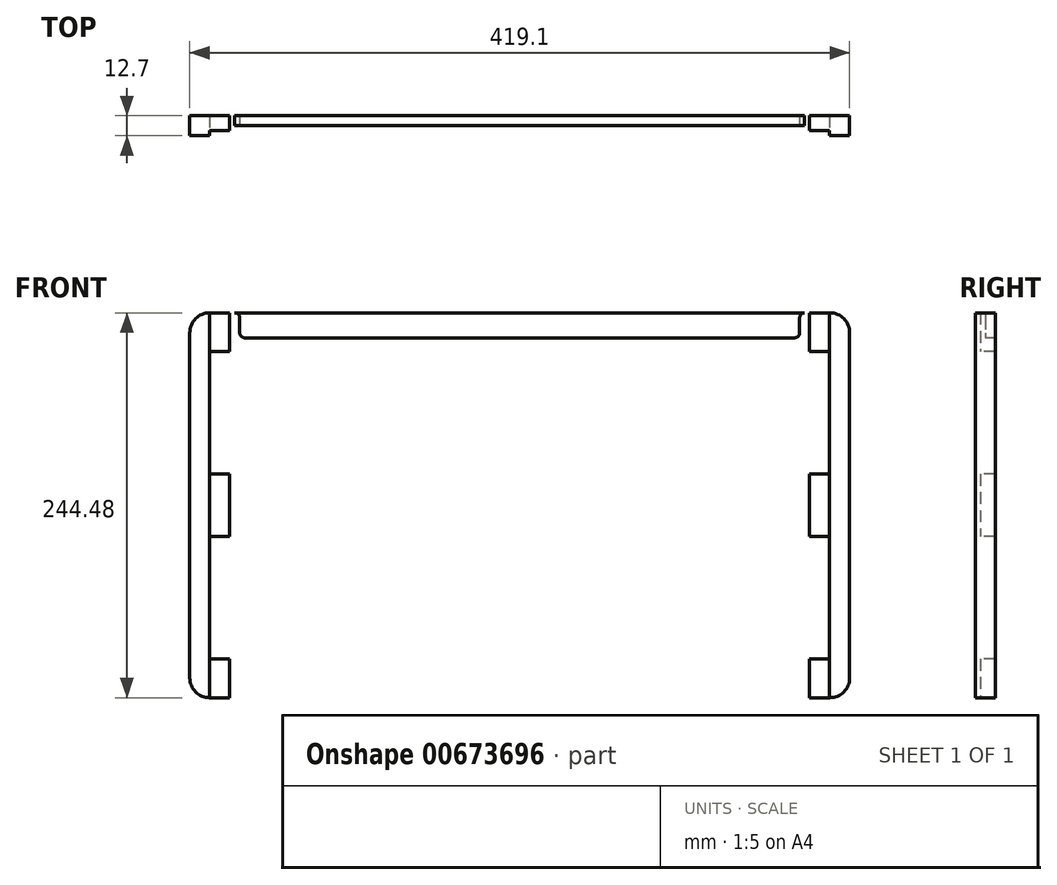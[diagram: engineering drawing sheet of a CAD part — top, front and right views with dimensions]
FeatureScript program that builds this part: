
annotation { "Feature Type Name" : "Feature", "Feature Type Description" : "" }
export const myFeature = defineFeature(function(context is Context, id is Id, definition is map)
    precondition{}
    {
        {
            var Q0;
            Q0=qCreatedBy(makeId("Front.planeOp"),FACE);
            var sketch = newSketch(context, id + "F0", { "sketchPlane" : qUnion([Q0])});
            skLineSegment(sketch, "E0.bottom", {"start": v(-196.85, 122.24) * mm, "end": v(-180.98, 122.24) * mm});
            skLineSegment(sketch, "E0.top", {"start": v(-196.85, -122.24) * mm, "end": v(196.85, -122.24) * mm});
            skLineSegment(sketch, "E0.left", {"start": v(-209.55, 109.54) * mm, "end": v(-209.55, -109.54) * mm});
            skLineSegment(sketch, "E0.right", {"start": v(209.55, 109.54) * mm, "end": v(209.55, -109.54) * mm});
            skPoint(sketch, "E0.middle", {"position": v(0, 0) * mm});
            skLineSegment(sketch, "E1", {"start": v(0, 122.24) * mm, "end": v(0, -122.24) * mm, "construction": true});
            skLineSegment(sketch, "E2", {"start": v(209.55, 0) * mm, "end": v(-209.55, 0) * mm, "construction": true});
            skLineSegment(sketch, "E3.left", {"start": v(-184.15, 122.24) * mm, "end": v(-184.15, -122.24) * mm});
            skLineSegment(sketch, "E3.right", {"start": v(184.15, 122.24) * mm, "end": v(184.15, -122.24) * mm});
            skLineSegment(sketch, "E4.bottom", {"start": v(-184.15, 97.63) * mm, "end": v(-196.85, 97.63) * mm});
            skLineSegment(sketch, "E4.top", {"start": v(-184.15, 19.84) * mm, "end": v(-196.85, 19.84) * mm});
            skLineSegment(sketch, "E4.left", {"start": v(-184.15, 97.63) * mm, "end": v(-184.15, 19.84) * mm});
            skLineSegment(sketch, "E4.right", {"start": v(-196.85, 97.63) * mm, "end": v(-196.85, 19.84) * mm});
            skLineSegment(sketch, "E5.MirrorCS", {"start": v(-184.15, -97.63) * mm, "end": v(-196.85, -97.63) * mm});
            skLineSegment(sketch, "E6.MirrorCS", {"start": v(-184.15, -19.84) * mm, "end": v(-196.85, -19.84) * mm});
            skLineSegment(sketch, "E7.MirrorCS", {"start": v(-184.15, -97.63) * mm, "end": v(-184.15, -19.84) * mm});
            skLineSegment(sketch, "E8.MirrorCS", {"start": v(-196.85, -97.63) * mm, "end": v(-196.85, -19.84) * mm});
            skLineSegment(sketch, "E9.MirrorCS", {"start": v(184.15, -97.63) * mm, "end": v(196.85, -97.63) * mm});
            skLineSegment(sketch, "E10.MirrorCS", {"start": v(196.85, 97.63) * mm, "end": v(196.85, 19.84) * mm});
            skLineSegment(sketch, "E11.MirrorCS", {"start": v(184.15, 97.63) * mm, "end": v(184.15, 19.84) * mm});
            skLineSegment(sketch, "E12.MirrorCS", {"start": v(184.15, -19.84) * mm, "end": v(196.85, -19.84) * mm});
            skLineSegment(sketch, "E13.MirrorCS", {"start": v(184.15, 19.84) * mm, "end": v(196.85, 19.84) * mm});
            skLineSegment(sketch, "E14.MirrorCS", {"start": v(184.15, -97.63) * mm, "end": v(184.15, -19.84) * mm});
            skLineSegment(sketch, "E15.MirrorCS", {"start": v(196.85, -97.63) * mm, "end": v(196.85, -19.84) * mm});
            skLineSegment(sketch, "E16.MirrorCS", {"start": v(184.15, 97.63) * mm, "end": v(196.85, 97.63) * mm});
            skPoint(sketch, "E17.visualSharp", {"position": v(-209.55, 122.24) * mm});
            skArc(sketch, "E17.filletArc", {"start": v(-196.85, 122.24) * mm, "mid": v(-205.83, 118.52) * mm, "end": v(-209.55, 109.54) * mm});
            skPoint(sketch, "E18.visualSharp", {"position": v(-209.55, -122.24) * mm});
            skArc(sketch, "E18.filletArc", {"start": v(-209.55, -109.54) * mm, "mid": v(-205.83, -118.52) * mm, "end": v(-196.85, -122.24) * mm});
            skPoint(sketch, "E19.visualSharp", {"position": v(209.55, -122.24) * mm});
            skArc(sketch, "E19.filletArc", {"start": v(196.85, -122.24) * mm, "mid": v(205.83, -118.52) * mm, "end": v(209.55, -109.54) * mm});
            skPoint(sketch, "E20.visualSharp", {"position": v(209.55, 122.24) * mm});
            skArc(sketch, "E20.filletArc", {"start": v(209.55, 109.54) * mm, "mid": v(205.83, 118.52) * mm, "end": v(196.85, 122.24) * mm});
            skLineSegment(sketch, "E21.top", {"start": v(-174.62, 106.36) * mm, "end": v(174.62, 106.36) * mm});
            skLineSegment(sketch, "E21.left", {"start": v(-177.8, 119.06) * mm, "end": v(-177.8, 109.54) * mm});
            skLineSegment(sketch, "E21.right", {"start": v(177.8, 119.06) * mm, "end": v(177.8, 109.54) * mm});
            skPoint(sketch, "E22.visualSharp", {"position": v(-177.8, 106.36) * mm});
            skArc(sketch, "E22.filletArc", {"start": v(-177.8, 109.54) * mm, "mid": v(-176.87, 107.3) * mm, "end": v(-174.62, 106.36) * mm});
            skArc(sketch, "E23.filletArc", {"start": v(-177.8, 119.06) * mm, "mid": v(-178.73, 121.3) * mm, "end": v(-180.98, 122.24) * mm});
            skPoint(sketch, "E24.visualSharp", {"position": v(177.8, 106.36) * mm});
            skArc(sketch, "E24.filletArc", {"start": v(174.62, 106.36) * mm, "mid": v(176.87, 107.3) * mm, "end": v(177.8, 109.54) * mm});
            skLineSegment(sketch, "E25", {"start": v(180.98, 122.24) * mm, "end": v(196.85, 122.24) * mm});
            skPoint(sketch, "E26.visualSharp", {"position": v(177.8, 122.24) * mm});
            skArc(sketch, "E26.filletArc", {"start": v(180.98, 122.24) * mm, "mid": v(178.73, 121.3) * mm, "end": v(177.8, 119.06) * mm});
            skLineSegment(sketch, "E27", {"start": v(-180.98, 122.24) * mm, "end": v(180.98, 122.24) * mm});
            skLineSegment(sketch, "E28", {"start": v(196.85, 122.24) * mm, "end": v(196.85, -122.24) * mm});
            skLineSegment(sketch, "E29", {"start": v(-196.85, 122.24) * mm, "end": v(-196.85, -122.24) * mm});
            skSolve(sketch);
        }
        {
            var Q0;
            Q0=makeQuery(id+"F0.imprint","IMPRINT",FACE,{"disambiguationData":[TD([[makeQuery(id+"F0.imprint","IMPRINT",EDGE,{"derivedFrom":sQuery(id+"F0.wireOp",EDGE,"E0.left")}),1.0]])]});
            var Q1;
            {var subQ5=sQuery(id+"F0.wireOp",EDGE,"E4.bottom");Q1=makeQuery(id+"F0.imprint","IMPRINT",FACE,{"disambiguationData":[TD([[makeQuery(id+"F0.imprint","IMPRINT",EDGE,{"derivedFrom":subQ5}),-1.0]])]});}
            var Q2;
            {var subQ0=sQuery(id+"F0.wireOp",EDGE,"E6.MirrorCS");Q2=makeQuery(id+"F0.imprint","IMPRINT",FACE,{"disambiguationData":[TD([[makeQuery(id+"F0.imprint","IMPRINT",EDGE,{"derivedFrom":subQ0}),-1.0]])]});}
            var Q3;
            {var subQ5=sQuery(id+"F0.wireOp",EDGE,"E5.MirrorCS");Q3=makeQuery(id+"F0.imprint","IMPRINT",FACE,{"disambiguationData":[TD([[makeQuery(id+"F0.imprint","IMPRINT",EDGE,{"derivedFrom":subQ5}),1.0]])]});}
            var Q4;
            {var subQ0=sQuery(id+"F0.wireOp",EDGE,"E7.MirrorCS");Q4=makeQuery(id+"F0.imprint","IMPRINT",FACE,{"disambiguationData":[TD([[makeQuery(id+"F0.imprint","IMPRINT",EDGE,{"derivedFrom":subQ0}),-1.0]])]});}
            var Q5;
            {var subQ5=sQuery(id+"F0.wireOp",EDGE,"E9.MirrorCS");Q5=makeQuery(id+"F0.imprint","IMPRINT",FACE,{"disambiguationData":[TD([[makeQuery(id+"F0.imprint","IMPRINT",EDGE,{"derivedFrom":subQ5}),-1.0]])]});}
            var Q6;
            Q6=makeQuery(id+"F0.imprint","IMPRINT",FACE,{"disambiguationData":[TD([[makeQuery(id+"F0.imprint","IMPRINT",EDGE,{"derivedFrom":sQuery(id+"F0.wireOp",EDGE,"E0.right")}),-1.0]])]});
            var Q7;
            {var subQ0=sQuery(id+"F0.wireOp",EDGE,"E12.MirrorCS");Q7=makeQuery(id+"F0.imprint","IMPRINT",FACE,{"disambiguationData":[TD([[makeQuery(id+"F0.imprint","IMPRINT",EDGE,{"derivedFrom":subQ0}),1.0]])]});}
            var Q8;
            {var subQ3=sQuery(id+"F0.wireOp",EDGE,"E16.MirrorCS");Q8=makeQuery(id+"F0.imprint","IMPRINT",FACE,{"disambiguationData":[TD([[makeQuery(id+"F0.imprint","IMPRINT",EDGE,{"derivedFrom":subQ3}),1.0]])]});}
            var Q9;
            Q9=makeQuery(id+"F0.imprint","IMPRINT",FACE,{"disambiguationData":[TD([[makeQuery(id+"F0.imprint","IMPRINT",EDGE,{"derivedFrom":sQuery(id+"F0.wireOp",EDGE,"E21.top")}),1.0]])]});
            extrude(context, id + "F1", {"entities" : qUnion([Q0, Q1, Q2, Q3, Q4, Q5, Q6, Q7, Q8, Q9]), "oppositeDirection" : true, "depth" : 12.7 * mm, "offsetDistance" : 25.4 * mm});
        }
        {
            var Q0;
            {var subQ5=sQuery(id+"F0.wireOp",EDGE,"E5.MirrorCS");Q0=makeQuery(id+"F0.imprint","IMPRINT",FACE,{"disambiguationData":[TD([[makeQuery(id+"F0.imprint","IMPRINT",EDGE,{"derivedFrom":subQ5}),1.0]])]});}
            var Q1;
            {var subQ0=sQuery(id+"F0.wireOp",EDGE,"E6.MirrorCS");Q1=makeQuery(id+"F0.imprint","IMPRINT",FACE,{"disambiguationData":[TD([[makeQuery(id+"F0.imprint","IMPRINT",EDGE,{"derivedFrom":subQ0}),-1.0]])]});}
            var Q2;
            {var subQ5=sQuery(id+"F0.wireOp",EDGE,"E9.MirrorCS");Q2=makeQuery(id+"F0.imprint","IMPRINT",FACE,{"disambiguationData":[TD([[makeQuery(id+"F0.imprint","IMPRINT",EDGE,{"derivedFrom":subQ5}),-1.0]])]});}
            var Q3;
            {var subQ0=sQuery(id+"F0.wireOp",EDGE,"E12.MirrorCS");Q3=makeQuery(id+"F0.imprint","IMPRINT",FACE,{"disambiguationData":[TD([[makeQuery(id+"F0.imprint","IMPRINT",EDGE,{"derivedFrom":subQ0}),1.0]])]});}
            var Q4;
            {var subQ3=sQuery(id+"F0.wireOp",EDGE,"E16.MirrorCS");Q4=makeQuery(id+"F0.imprint","IMPRINT",FACE,{"disambiguationData":[TD([[makeQuery(id+"F0.imprint","IMPRINT",EDGE,{"derivedFrom":subQ3}),1.0]])]});}
            var Q5;
            {var subQ5=sQuery(id+"F0.wireOp",EDGE,"E4.bottom");Q5=makeQuery(id+"F0.imprint","IMPRINT",FACE,{"disambiguationData":[TD([[makeQuery(id+"F0.imprint","IMPRINT",EDGE,{"derivedFrom":subQ5}),-1.0]])]});}
            extrude(context, id + "F2", {"entities" : qUnion([Q0, Q1, Q2, Q3, Q4, Q5]), "operationType" : NewBodyOperationType.REMOVE, "oppositeDirection" : true, "depth" : 3.17 * mm, "offsetDistance" : 25.4 * mm});
        }
        {
            var Q0;
            Q0=makeQuery(id+"F0.imprint","IMPRINT",FACE,{"disambiguationData":[TD([[makeQuery(id+"F0.imprint","IMPRINT",EDGE,{"derivedFrom":sQuery(id+"F0.wireOp",EDGE,"E21.top")}),1.0]])]});
            extrude(context, id + "F3", {"entities" : qUnion([Q0]), "operationType" : NewBodyOperationType.REMOVE, "oppositeDirection" : true, "depth" : 6.35 * mm, "offsetDistance" : 25.4 * mm});
        }
    });
